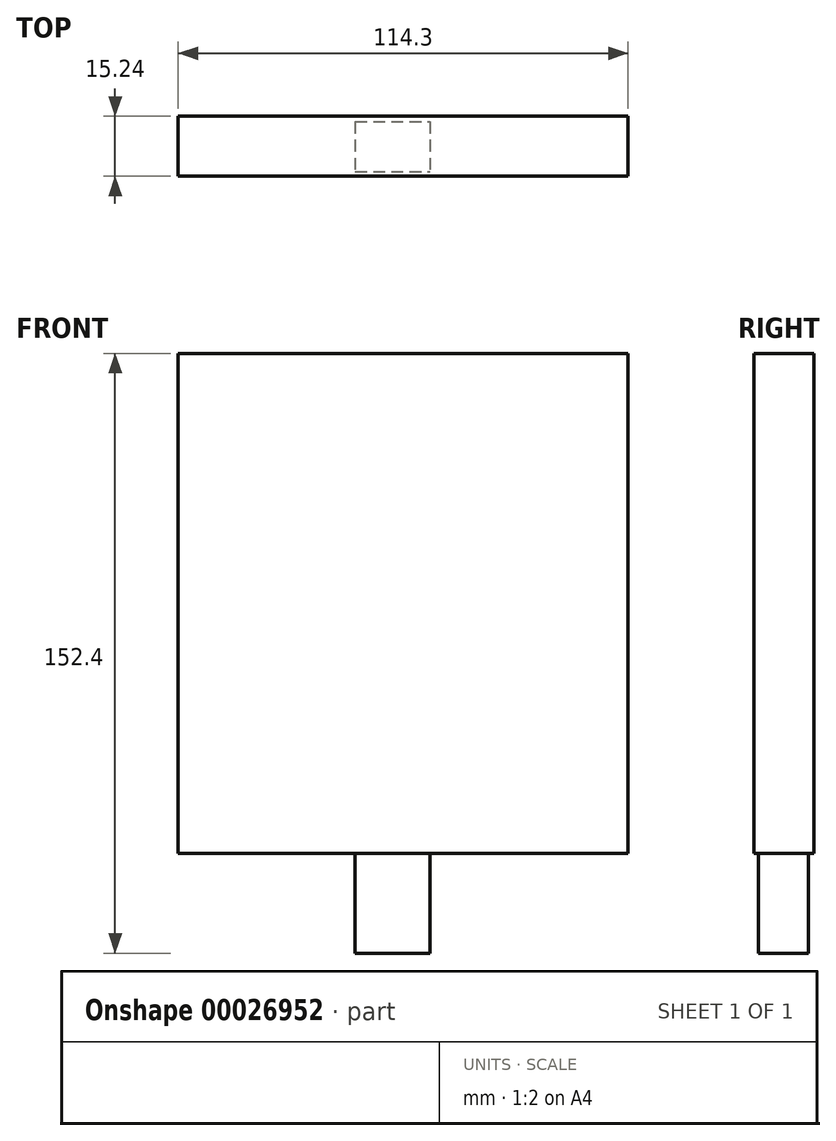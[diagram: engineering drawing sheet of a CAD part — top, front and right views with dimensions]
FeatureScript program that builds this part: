
annotation { "Feature Type Name" : "Feature", "Feature Type Description" : "" }
export const myFeature = defineFeature(function(context is Context, id is Id, definition is map)
    precondition{}
    {
        {
            var Q0;
            Q0=qCreatedBy(makeId("Top.planeOp"),FACE);
            var sketch = newSketch(context, id + "F0", { "sketchPlane" : qUnion([Q0])});
            skLineSegment(sketch, "E0.bottom", {"start": v(-9.53, 6.98) * mm, "end": v(9.52, 6.98) * mm});
            skLineSegment(sketch, "E0.top", {"start": v(-9.53, -5.72) * mm, "end": v(9.52, -5.71) * mm});
            skLineSegment(sketch, "E0.left", {"start": v(-9.53, 6.98) * mm, "end": v(-9.53, -5.72) * mm});
            skLineSegment(sketch, "E0.right", {"start": v(9.52, 6.98) * mm, "end": v(9.52, -5.72) * mm});
            skSolve(sketch);
        }
        {
            var Q0;
            Q0=makeQuery(id+"F0.imprint","IMPRINT",FACE,{"disambiguationData":[TD([[makeQuery(id+"F0.imprint","IMPRINT",EDGE,{"derivedFrom":sQuery(id+"F0.wireOp",EDGE,"E0.bottom")}),-1.0]])]});
            extrude(context, id + "F1", {"entities" : qUnion([Q0]), "depth" : 25.4 * mm});
        }
        {
            var Q0;
            Q0=qCreatedBy(makeId("Top.planeOp"),FACE);
            cPlane(context, id + "F2", {"entities" : qUnion([Q0]), "cplaneType" : CPlaneType.OFFSET, "offset" : 25.4 * mm, "width" : 152.4 * mm, "height" : 152.4 * mm});
        }
        {
            var Q0;
            Q0=qCreatedBy(id+"F2.planeOp",FACE);
            var sketch = newSketch(context, id + "F3", { "sketchPlane" : qUnion([Q0])});
            skLineSegment(sketch, "E1.bottom", {"start": v(-54.49, 8.35) * mm, "end": v(59.81, 8.35) * mm});
            skLineSegment(sketch, "E1.top", {"start": v(-54.49, -6.9) * mm, "end": v(59.81, -6.9) * mm});
            skLineSegment(sketch, "E1.left", {"start": v(-54.49, 8.35) * mm, "end": v(-54.49, -6.9) * mm});
            skLineSegment(sketch, "E1.right", {"start": v(59.81, 8.35) * mm, "end": v(59.81, -6.9) * mm});
            skSolve(sketch);
        }
        {
            var Q0;
            Q0=makeQuery(id+"F3.imprint","IMPRINT",FACE,{"disambiguationData":[TD([[makeQuery(id+"F3.imprint","IMPRINT",EDGE,{"derivedFrom":sQuery(id+"F3.wireOp",EDGE,"E1.bottom")}),-1.0]])]});
            extrude(context, id + "F4", {"entities" : qUnion([Q0]), "operationType" : NewBodyOperationType.ADD, "depth" : 127 * mm});
        }
        {
            var Q0;
            Q0=qCreatedBy(makeId("Front.planeOp"),FACE);
            cPlane(context, id + "F5", {"entities" : qUnion([Q0]), "cplaneType" : CPlaneType.OFFSET, "offset" : 38.1 * mm, "width" : 152.4 * mm, "height" : 152.4 * mm});
        }
        {
            var Q0;
            Q0=qCreatedBy(id+"F5.planeOp",FACE);
            var sketch = newSketch(context, id + "F6", { "sketchPlane" : qUnion([Q0])});
            skLineSegment(sketch, "E2", {"start": v(0, 317.18) * mm, "end": v(0, 279.08) * mm});
            skArc(sketch, "E3", {"start": v(0, 279.08) * mm, "mid": v(19.05, 298.13) * mm, "end": v(0, 317.18) * mm});
            skSolve(sketch);
        }
        {
            var Q0;
            Q0=qSketchRegion(id+"F6",true);
            var Q1;
            Q1=sQuery(id+"F6.wireOp",EDGE,"E2");
            revolve(context, id + "F7", {"operationType" : NewBodyOperationType.REMOVE, "entities" : qUnion([Q0]), "axis" : qUnion([Q1]), "revolveType" : RevolveType.FULL, "oppositeDirection" : true});
        }
        {
            var Q0;
            Q0=qCreatedBy(makeId("Top.planeOp"),FACE);
            cPlane(context, id + "F8", {"entities" : qUnion([Q0]), "cplaneType" : CPlaneType.OFFSET, "offset" : 266.7 * mm, "width" : 152.4 * mm, "height" : 152.4 * mm});
        }
        {
            var Q0;
            Q0=qCreatedBy(id+"F8.planeOp",FACE);
            var sketch = newSketch(context, id + "F9", { "sketchPlane" : qUnion([Q0])});
            skLineSegment(sketch, "E4", {"start": v(0, 11.13) * mm, "end": v(0, -14.27) * mm});
            skArc(sketch, "E5", {"start": v(0, -14.27) * mm, "mid": v(12.7, -1.57) * mm, "end": v(0, 11.13) * mm});
            skSolve(sketch);
        }
        {
            var Q0;
            Q0=qSketchRegion(id+"F9",true);
            var Q1;
            Q1=sQuery(id+"F9.wireOp",EDGE,"E4");
            revolve(context, id + "F10", {"operationType" : NewBodyOperationType.REMOVE, "entities" : qUnion([Q0]), "axis" : qUnion([Q1]), "revolveType" : RevolveType.FULL, "oppositeDirection" : true});
        }
    });
